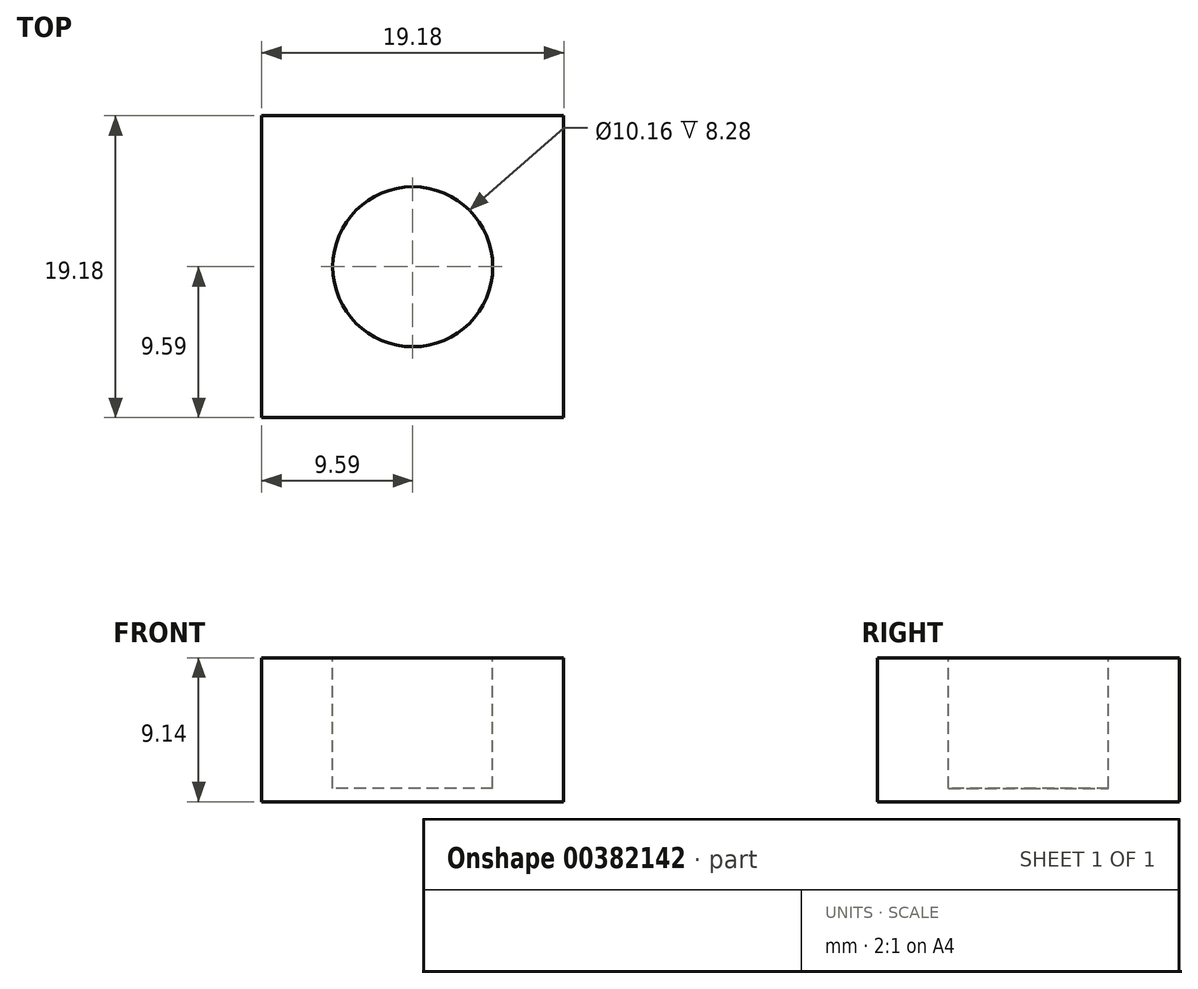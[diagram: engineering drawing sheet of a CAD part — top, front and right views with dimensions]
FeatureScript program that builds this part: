
annotation { "Feature Type Name" : "Feature", "Feature Type Description" : "" }
export const myFeature = defineFeature(function(context is Context, id is Id, definition is map)
    precondition{}
    {
        {
            var Q0;
            Q0=qCreatedBy(makeId("Top.planeOp"),FACE);
            var sketch = newSketch(context, id + "F0", { "sketchPlane" : qUnion([Q0])});
            skLineSegment(sketch, "E0.bottom", {"start": v(9.59, -9.59) * mm, "end": v(-9.59, -9.59) * mm});
            skLineSegment(sketch, "E0.top", {"start": v(9.59, 9.59) * mm, "end": v(-9.59, 9.59) * mm});
            skLineSegment(sketch, "E0.left", {"start": v(9.59, -9.59) * mm, "end": v(9.59, 9.59) * mm});
            skLineSegment(sketch, "E0.right", {"start": v(-9.59, -9.59) * mm, "end": v(-9.59, 9.59) * mm});
            skPoint(sketch, "E0.middle", {"position": v(0, 0) * mm});
            skSolve(sketch);
        }
        {
            var Q0;
            Q0=makeQuery(id+"F0.imprint","IMPRINT",FACE,{"disambiguationData":[TD([[makeQuery(id+"F0.imprint","IMPRINT",EDGE,{"derivedFrom":sQuery(id+"F0.wireOp",EDGE,"E0.bottom")}),-1.0]])]});
            extrude(context, id + "F1", {"entities" : qUnion([Q0]), "oppositeDirection" : true, "depth" : 9.14 * mm});
        }
        {
            var Q0;
            Q0=makeQuery(id+"F1.opExtrude","CAP_FACE",FACE,{"disambiguationData":[OSD([sQuery(id+"F0.wireOp",EDGE,"E0.bottom"),sQuery(id+"F0.wireOp",EDGE,"E0.top"),sQuery(id+"F0.wireOp",EDGE,"E0.left"),sQuery(id+"F0.wireOp",EDGE,"E0.right")])],"isStart":true});
            var sketch = newSketch(context, id + "F2", { "sketchPlane" : qUnion([Q0])});
            skPoint(sketch, "E1.0.midPoint", {"position": v(0, -13) * mm});
            skCircle(sketch, "E2", {"center": v(0, 0) * mm, "radius": 5.08 * mm});
            skSolve(sketch);
        }
        {
            var Q0;
            Q0=makeQuery(id+"F2.imprint","IMPRINT",FACE,{"disambiguationData":[TD([[makeQuery(id+"F2.imprint","IMPRINT",EDGE,{"derivedFrom":sQuery(id+"F2.wireOp",EDGE,"E2")}),1.0]])]});
            extrude(context, id + "F3", {"entities" : qUnion([Q0]), "operationType" : NewBodyOperationType.REMOVE, "oppositeDirection" : true, "depth" : 8.28 * mm});
        }
    });
